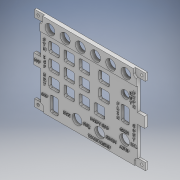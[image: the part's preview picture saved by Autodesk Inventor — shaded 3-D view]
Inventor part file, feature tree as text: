
AUTODESK INVENTOR PART (.ipt)
format: ipt  version: 2022 (Build 260153000, 153)  size: 1,637,376 bytes
history: native  units: in
note: dims shown in document units (in); Inventor stores cm internally (conversion verified against a paired STEP export)
features: sketch x5, extrude x5, fillet x4
ambient origin geometry x8: Origin, YZ Plane, XZ Plane, XY Plane, X Axis, Y Axis, Z Axis, Center Point
bodies: Solid1 (feature_tree)
feature tree (14):
  sketch  "Sketch1"  dims[d1=0.75in d2=0.75in]
  extrude  "Extrusion1"  Depth=0.75in
  extrude  "Extrusion2"  Depth=0.75in
  fillet  "Fillet1"  Radius=0.75in
  fillet  "Fillet2"  Radius=4.1732in
  fillet  "Fillet3"  Radius=0.5039in
  fillet  "Fillet4"  Radius=0.3949in
  sketch  "Sketch2"  dims[d3=0.75in d4=0.75in d5=0.75in d6=4.1732in d8=0.5039in d10=0.3949in]
  extrude  "Extrusion3"  Depth=0.3543in
  extrude  "Extrusion4"  Depth=0.5118in
  extrude  "Extrusion5"  Depth=0.0354in
  sketch  "Sketch4"  dims[d13=1.4764in d14=0.5118in]
  sketch  "Sketch5"  dims[d15=1.4764in d16=0.3543in d17=0.2043in d18=0.7614in d19=0.2524in d20=0.5173in d21=0.2315in d22=0.5173in d23=0.2315in d24=0.5173in d25=0.3937in d26=0.515in d27=0.2339in d28=0.515in d29=0.2339in d30=0.5154in d31=0.4528in d32=0.515in d33=0.2339in d34=0.5902in d36=0.4898in d37=0.4898in d38=0.4898in d39=0.4898in d40=0.4898in d41=0.4898in d42=0.3543in d43=0.5039in d44=0.3543in d45=0.8516in d46=0.7169in d47=0.7614in d49=0.4898in d50=0.6283in d51=1.2299in d52=1.1205in d53=0.9236in d54=0.389in d55=0.5441in d56=0.4898in d57=0.389in d58=0.4787in d60=0.6559in d61=0.389in d62=0.1378in d63=0.0in d64=0.1969in d65=0.0in d66=0.0787in d67=0.0787in d68=0.0787in d69=0.0787in d71=90.0deg d72=2.0866in d73=0.1299in d74=0.0984in d75=0.0in d76=0.7141in d77=0.0in d78=0.315in d79=0.315in d80=0.315in d81=0.315in d82=0.315in d83=0.315in d84=0.315in d85=0.315in d89=0.0354in d90=0.0in d91=0.515in]
  sketch  "Sketch3"  dims[d11=0.3543in d12=0.3543in]
